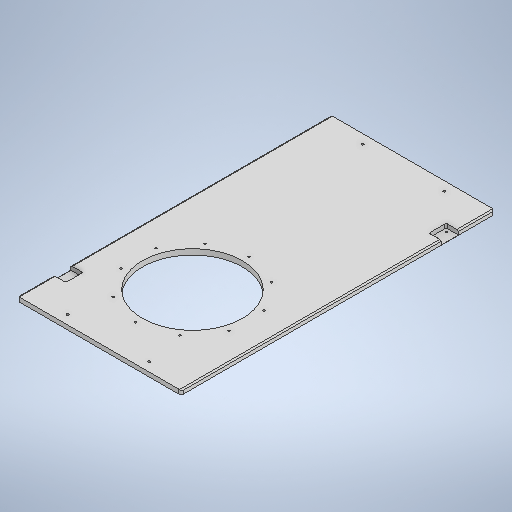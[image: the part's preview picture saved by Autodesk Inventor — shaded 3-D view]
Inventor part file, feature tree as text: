
AUTODESK INVENTOR PART (.ipt)
format: ipt  version: 2025 (Build 290162000, 162)  size: 410,624 bytes
history: native  units: in
note: dims shown in document units (in); Inventor stores cm internally (conversion verified against a paired STEP export)
features: sketch x9, extrude x5, hole x3, chamfer x3, plane x2, fillet x2, pattern_circular x1
ambient origin geometry x8: Origin, YZ Plane, XZ Plane, XY Plane, X Axis, Y Axis, Z Axis, Center Point
bodies: Solid1 (feature_tree)
feature tree (25):
  extrude  "Base Cover"  Depth=27.1654in
  sketch  "Sketch2"  dims[d2=0.4724in d3=0.0in d4=8.0709in]
  extrude  "Cylinder Hole"  Depth=0.4724in
  plane  "Work Plane1"
  hole  "Handle Holes"  [1 undecoded]
  sketch  "Sketch7"  dims[d8=10.6299in d50=5.9055in d55=7.0625in]
  plane  "Work Plane2"
  hole  "Cylinder Mount Holes"  [1 undecoded]
  sketch  "Sketch9"  dims[d57=0.1936in d58=0.1969in d59=0.1575in d60=0.0787in d61=90.0deg d62=0.1969in d63=0.8108in]
  fillet  "Rounded Side Corners"  Radius=7.0625in
  chamfer  "Chamfer1"  Distance=1.063in
  chamfer  "Chamfer2"  Distance=1.063in
  extrude  "Magnet Seats"  Depth=0.3937in
  hole  "Magnet Holes"  [1 undecoded]
  chamfer  "Chamfer5"  Distance=3.1102in
  fillet  "Rounded Bottom Corners"  Radius=3.1102in
  extrude  "Extrusion14"  Depth=0.3937in
  extrude  "Extrusion15"  Depth=0.3937in TaperAngle=45.0deg
  pattern_circular  "Circular Pattern1"  Angle=45.0deg  [1 undecoded]
  sketch  "Sketch1"  dims[d0=14.1732in d1=27.1654in]
  sketch  "Sketch6"  dims[d5=8.6614in d6=0.0in d7=0.0in]
  sketch  "Sketch8"  dims[d56=25.5906in]
  sketch  "Sketch11"  dims[d64=10.3543in]
  sketch  "Sketch18"  dims[d65=10.6299in]
  sketch  "Sketch19"  dims[d68=9.8425in d74=0.1628in d75=0.3937in d76=0.1575in d77=0.0787in d78=90.0deg d79=0.3937in d80=0.8108in d82=1.063in d83=1.063in d84=1.4961in d85=1.4961in d86=3.1102in d87=3.1102in d88=0.1969in d89=0.0984in d90=0.0787in d91=45.0deg d92=0.0984in d93=0.0787in d94=45.0deg d95=0.1181in d96=0.1181in d97=0.3543in d98=0.0in d109=0.748in d110=0.315in d111=0.8661in d112=0.748in d113=0.1299in d114=0.1299in d115=0.1299in d116=0.1299in d118=0.315in d119=0.8661in d120=0.748in d121=0.748in d122=0.1276in d123=0.315in d124=0.1575in d125=0.0787in d126=90.0deg d127=0.315in d128=0.8108in d129=0.0138in d130=0.0787in d131=45.0deg d230=0.2756in d243=0.1378in d244=0.0787in d245=0.3848in d246=0.0in d247=0.1378in d248=0.0787in d249=0.3937in d250=0.0in d278=0.1575in d279=3.937in d280=360.0deg d26=0.0394in d27=0.0394in d28=0.0394in d29=0.0059in d30=0.0098in d31=0.0148in d32=0.5635in d33=0.0295in d34=0.8108in d35=0.0025in d36=0.0295in d37=0.0148in d66=0.0197in d67=0.0344in d251=0.0394in d252=0.0394in d253=0.0394in d254=0.0059in d255=0.0098in d256=0.0148in d257=0.5635in d258=0.0295in d259=0.8108in d260=0.0025in d261=0.0295in d262=0.0148in d263=0.0394in d264=0.0394in d265=0.0059in d266=0.0098in d267=0.0148in d268=0.5635in d269=0.0295in d270=0.8108in d271=0.0025in d272=0.0295in d273=0.0148in]
note: 4 required parameter values undecoded (feature->parameter linkage not recoverable at this tier; creation-order binding heuristic only, values carry confidence <= 0.55)
